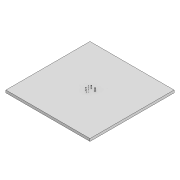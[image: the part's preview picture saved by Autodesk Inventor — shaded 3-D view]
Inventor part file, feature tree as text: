
AUTODESK INVENTOR PART (.ipt)
format: ipt  version: 2021 (Build 250183000, 183)  size: 107,008 bytes
history: native  units: in
note: dims shown in document units (in); Inventor stores cm internally (conversion verified against a paired STEP export)
features: extrude x2, sketch x2, projected_geometry x1
ambient origin geometry x8: Origin, YZ Plane, XZ Plane, XY Plane, X Axis, Y Axis, Z Axis, Center Point
bodies: Solid1 (feature_tree)
feature tree (5):
  extrude  "Extrusion1"  Depth=3937.0079in
  extrude  "Extrusion2"  Depth=118.1102in
  sketch  "Sketch1"  dims[d0=3937.0079in d1=3937.0079in]
  sketch  "Sketch2"  dims[d2=118.1102in d3=0.0in d4=39.3701in d5=118.1102in d6=78.7402in d7=15.748in d8=118.1102in d9=59.0551in d10=59.0551in d11=78.7402in d13=157.4803in d14=15.748in d15=39.3701in d16=118.1102in d17=39.3701in d18=98.4252in d19=39.3701in d20=19.685in d21=196.8504in d22=23.622in d23=118.1102in d24=0.0in]
  projected_geometry  "Projected Loop1"
